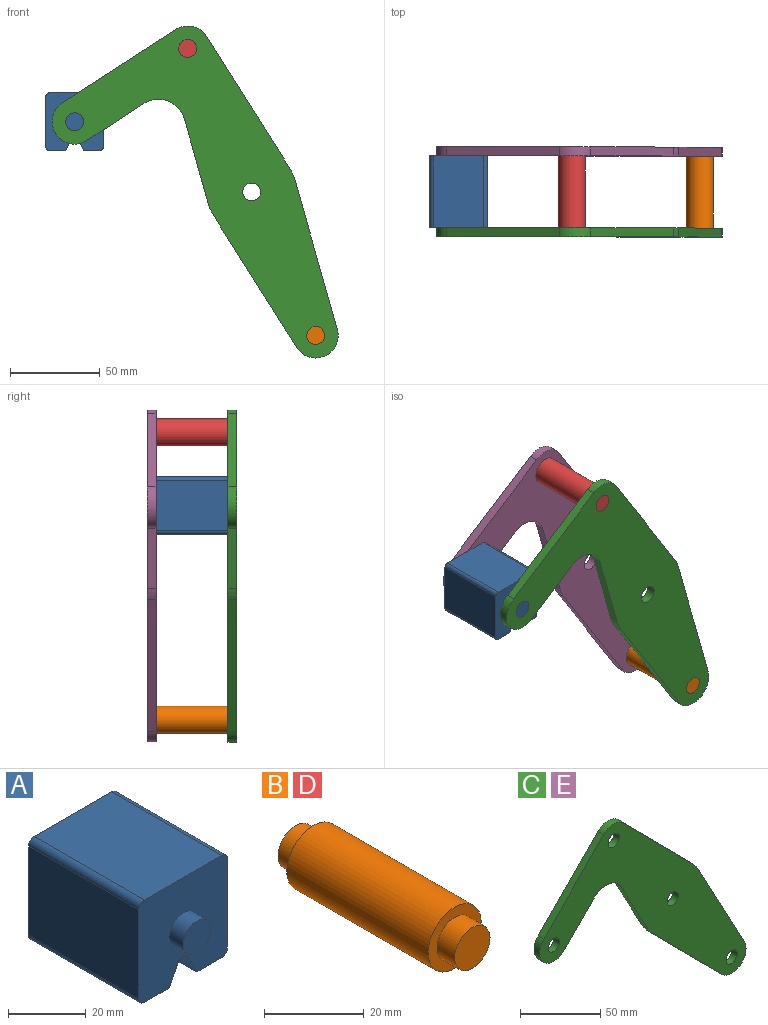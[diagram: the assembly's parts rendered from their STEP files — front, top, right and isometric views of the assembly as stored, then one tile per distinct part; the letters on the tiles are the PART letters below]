
ASSEMBLY  parts=5 mates=3
PART A: 18 faces, bbox 32.1x50x32.1 mm
  f0: plane 40x28.08mm, normal (1,0,0), area 1123.1mm2, adj f4,f10,f13,f14
  f1: plane 40x9.04mm, normal (0,0,-1), area 361.6mm2, adj f2,f4,f10,f14
  f2: plane 40x6.42mm, normal (-0.89,0,-0.45), area 287.2mm2, adj f1,f4,f10,f15
  f3: plane 40x6.42mm, normal (0.89,0,-0.45), area 287.2mm2, adj f4,f5,f10,f15
  f4: plane 32.08x32.08mm, normal (0,-1,0), area 900.6mm2, adj f0,f1,f2,f3,f5,f6,f7,f9
  f5: plane 40x9.04mm, normal (0,0,-1), area 361.6mm2, adj f3,f4,f10,f16
  f6: plane 40x28.08mm, normal (0,0,1), area 1123.1mm2, adj f4,f10,f13,f17
  f7: plane 40x28.08mm, normal (-1,0,0), area 1123.1mm2, adj f4,f10,f16,f17
  f8: plane 10x10mm, normal (0,-1,0), area 78.5mm2, adj f9
  f9: cylinder r=5mm len=10mm, axis (0,1,0), area 157.1mm2, adj f4,f8
  f10: plane 32.08x32.08mm, normal (0,1,0), area 900.6mm2, adj f0,f1,f2,f3,f5,f6,f7,f12
  f11: plane 10x10mm, normal (0,1,0), area 78.5mm2, adj f12
  f12: cylinder r=5mm len=10mm, axis (0,-1,0), area 157.1mm2, adj f10,f11
  f13: cylinder r=2mm len=40mm, axis (0,1,0), area 125.7mm2, adj f0,f4,f6,f10
  f14: cylinder r=2mm len=40mm, axis (0,-1,0), area 125.7mm2, adj f0,f1,f4,f10
  f15: cylinder r=2mm len=40mm, axis (0,1,0), area 177.1mm2, adj f2,f3,f4,f10
  f16: cylinder r=2mm len=40mm, axis (0,1,0), area 125.7mm2, adj f4,f5,f7,f10
  f17: cylinder r=2mm len=40mm, axis (0,-1,0), area 125.7mm2, adj f4,f6,f7,f10
PART B: 7 faces, bbox 15x50x15 mm
  f0: cylinder r=7.5mm len=40mm, axis (0,-1,0), area 1885mm2, adj f2,f5
  f1: cylinder r=5mm len=10mm, axis (0,1,0), area 157.1mm2, adj f2,f3
  f2: plane 15x15mm, normal (0,-1,0), area 98.2mm2, adj f0,f1
  f3: plane 10x10mm, normal (0,-1,0), area 78.5mm2, adj f1
  f4: cylinder r=5mm len=10mm, axis (0,-1,0), area 157.1mm2, adj f5,f6
  f5: plane 15x15mm, normal (0,1,0), area 98.2mm2, adj f0,f4
  f6: plane 10x10mm, normal (0,1,0), area 78.5mm2, adj f4
PART C: 18 faces, bbox 181.7x5x165.8 mm
  f0: plane 43.49x23.35mm, normal (-0.88,0,-0.47), area 246.8mm2, adj f1,f14,f16,f17
  f1: cylinder r=25mm len=5.75mm, axis (0,1,0), area 35.8mm2, adj f0,f2,f16,f17
  f2: plane 61.6x60.87mm, normal (-0.71,0,-0.7), area 433mm2, adj f1,f3,f16,f17
  f3: cylinder r=12.5mm len=21.39mm, axis (0,1,0), area 178.4mm2, adj f2,f4,f16,f17
  f4: plane 76.3x40.96mm, normal (0.88,0,0.47), area 433mm2, adj f3,f5,f16,f17
  f5: cylinder r=25mm len=5.75mm, axis (0,1,0), area 35.8mm2, adj f4,f6,f16,f17
  f6: plane 61.6x60.87mm, normal (0.71,0,0.7), area 433mm2, adj f5,f7,f16,f17
  f7: cylinder r=12.5mm len=17.78mm, axis (0,1,0), area 98.9mm2, adj f6,f8,f16,f17
  f8: plane 53.35x52.71mm, normal (-0.71,0,0.7), area 375mm2, adj f7,f9,f16,f17
  f9: cylinder r=12.5mm len=21.39mm, axis (0,1,0), area 196.3mm2, adj f8,f10,f16,f17
  f10: plane 26.86x26.54mm, normal (0.71,0,-0.7), area 188.8mm2, adj f9,f14,f16,f17
  f11: cylinder r=5mm len=10mm, axis (0,1,0), area 157.1mm2, adj f16,f17
  f12: cylinder r=5mm len=10mm, axis (0,1,0), area 157.1mm2, adj f16,f17
  f13: cylinder r=5mm len=10mm, axis (0,1,0), area 157.1mm2, adj f16,f17
  f14: cylinder r=15mm len=23.89mm, axis (0,1,0), area 140.2mm2, adj f0,f10,f16,f17
  f15: cylinder r=5mm len=10mm, axis (0,1,0), area 157.1mm2, adj f16,f17
  f16: plane 181.66x165.78mm, normal (0,-1,0), area 8710.1mm2, adj f0,f1,f2,f3,f4,f5,f6,f7
  f17: plane 181.66x165.78mm, normal (0,1,0), area 8710.1mm2, adj f0,f1,f2,f3,f4,f5,f6,f7
PART D: same geometry as B
PART E: same geometry as C
PLACE A t=(6.11,-20,22.1)mm
PLACE B rot(axis=(0,1,0),12.4deg) t=(71.26,-20,-159.83)mm
PLACE C rot(axis=(0,1,0),12.4deg) t=(0,-20,0)mm fixed
PLACE D rot(axis=(0,1,0),12.4deg) t=(0,-20,0)mm
PLACE E rot(axis=(0,1,0),12.4deg) t=(0,25,0)mm
MATE fastened E.f7 <-> D.f0  axis (0,1,0) through (-35.63,25,79.92)mm
MATE fastened B.f0 <-> C.f3  axis (0,-1,0) through (35.63,-25,-79.92)mm
MATE revolute A.f9 <-> C.f9  axis (0,-1,0) through (-98.58,-25,39.14)mm
